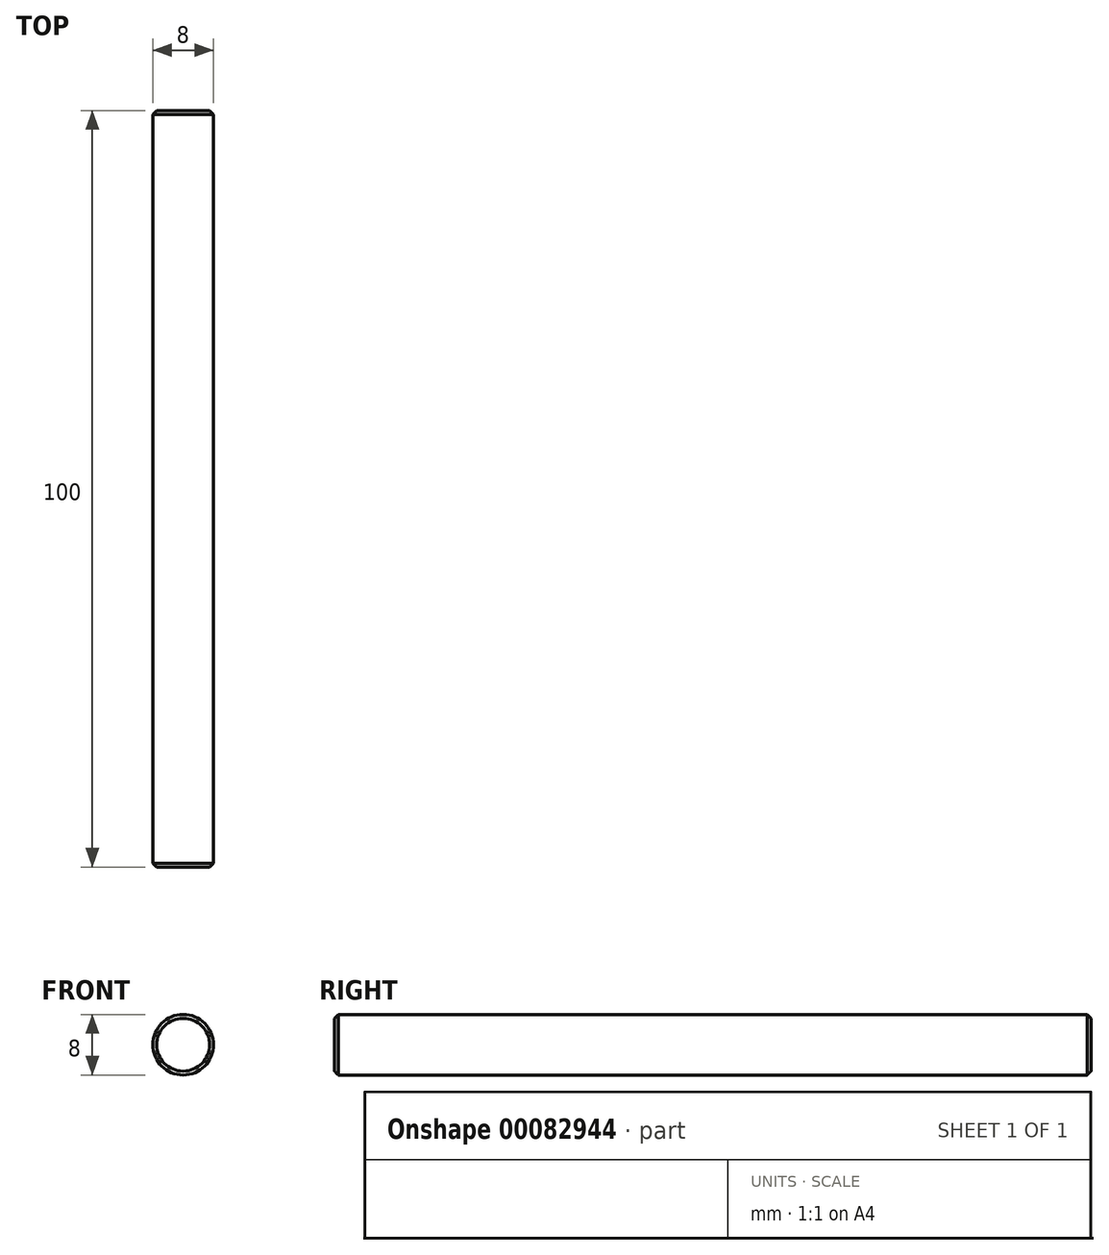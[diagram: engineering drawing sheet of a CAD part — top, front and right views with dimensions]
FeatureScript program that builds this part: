
annotation { "Feature Type Name" : "Feature", "Feature Type Description" : "" }
export const myFeature = defineFeature(function(context is Context, id is Id, definition is map)
    precondition{}
    {
        {
            var Q0;
            Q0=qCreatedBy(makeId("Front.planeOp"),FACE);
            var sketch = newSketch(context, id + "F0", { "sketchPlane" : qUnion([Q0])});
            skCircle(sketch, "E0", {"center": v(0, 0) * mm, "radius": 4 * mm});
            skSolve(sketch);
        }
        {
            var Q0;
            Q0=makeQuery(id+"F0.imprint","IMPRINT",FACE,{"disambiguationData":[TD([[makeQuery(id+"F0.imprint","IMPRINT",EDGE,{"derivedFrom":sQuery(id+"F0.wireOp",EDGE,"E0")}),1.0]])]});
            var Q1;
            Q1=sQuery(id+"F0.wireOp",EDGE,"E0");
            extrude(context, id + "F1", {"entities" : qUnion([Q0]), "surfaceEntities" : qUnion([Q1]), "depth" : 100 * mm});
        }
        {
            var Q0;
            Q0=makeQuery(id+"F1.opExtrude","CAP_EDGE",EDGE,{"disambiguationData":[OSD([sQuery(id+"F0.wireOp",EDGE,"E0")])],"isStart":false});
            var Q1;
            Q1=makeQuery(id+"F1.opExtrude","CAP_EDGE",EDGE,{"disambiguationData":[OSD([sQuery(id+"F0.wireOp",EDGE,"E0")])],"isStart":true});
            chamfer(context, id + "F2", {"entities" : qUnion([Q0, Q1]), "width" : 0.5 * mm, "tangentPropagation" : true});
        }
    });
